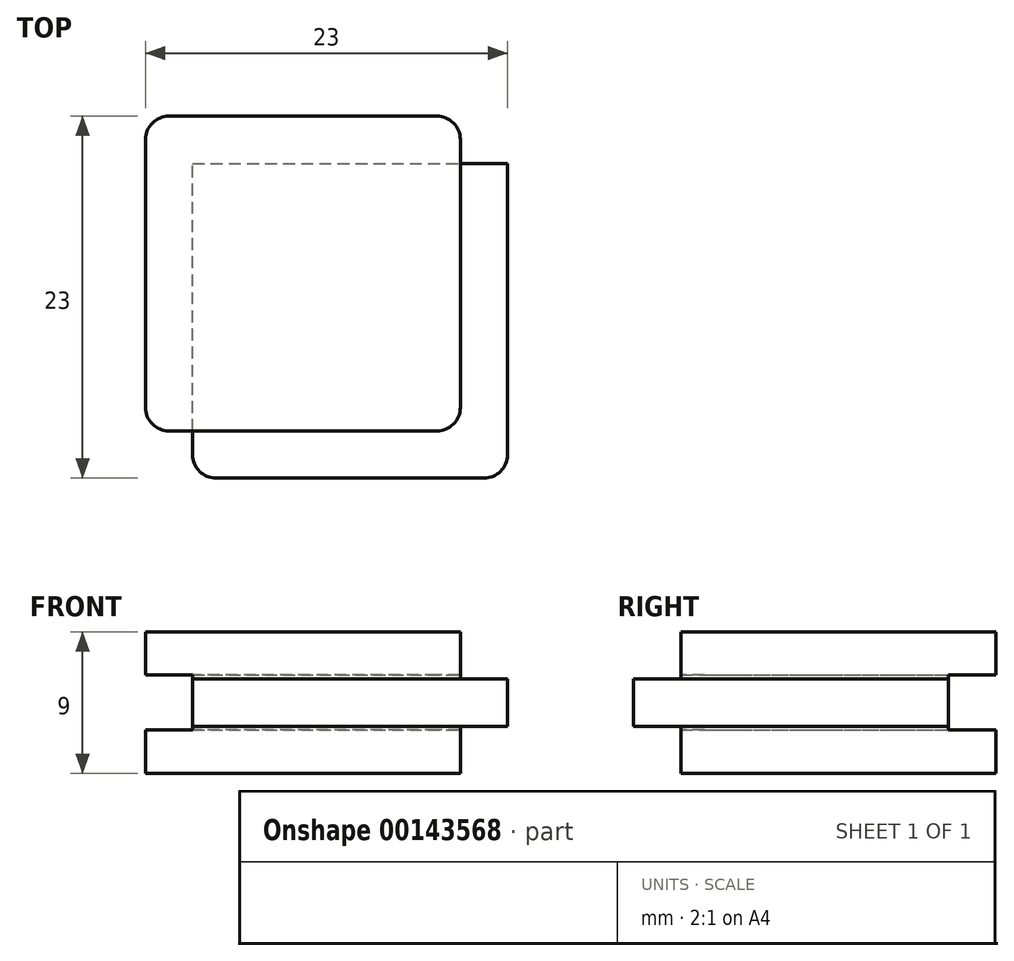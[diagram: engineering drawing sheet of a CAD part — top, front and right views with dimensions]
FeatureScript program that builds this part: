
annotation { "Feature Type Name" : "Feature", "Feature Type Description" : "" }
export const myFeature = defineFeature(function(context is Context, id is Id, definition is map)
    precondition{}
    {
        {
            var Q0;
            Q0=qCreatedBy(makeId("Front.planeOp"),FACE);
            var sketch = newSketch(context, id + "F0", { "sketchPlane" : qUnion([Q0])});
            skLineSegment(sketch, "E0.bottom", {"start": v(10, 4.5) * mm, "end": v(-10, 4.5) * mm});
            skLineSegment(sketch, "E0.top", {"start": v(10, -4.5) * mm, "end": v(-10, -4.5) * mm});
            skLineSegment(sketch, "E0.left", {"start": v(10, 4.5) * mm, "end": v(10, -4.5) * mm});
            skLineSegment(sketch, "E0.right", {"start": v(-10, 4.5) * mm, "end": v(-10, -4.5) * mm});
            skPoint(sketch, "E0.middle", {"position": v(0, 0) * mm});
            skLineSegment(sketch, "E1.bottom", {"start": v(13, 1.5) * mm, "end": v(7, 1.5) * mm});
            skLineSegment(sketch, "E1.top", {"start": v(13, -1.5) * mm, "end": v(7, -1.5) * mm});
            skLineSegment(sketch, "E1.left", {"start": v(13, 1.5) * mm, "end": v(13, -1.5) * mm});
            skLineSegment(sketch, "E1.right", {"start": v(7, 1.5) * mm, "end": v(7, -1.5) * mm});
            skPoint(sketch, "E1.middle", {"position": v(10, 0) * mm});
            skLineSegment(sketch, "E2.bottom", {"start": v(7, 1.5) * mm, "end": v(-7, 1.5) * mm});
            skLineSegment(sketch, "E2.top", {"start": v(7, -1.5) * mm, "end": v(-7, -1.5) * mm});
            skLineSegment(sketch, "E2.right", {"start": v(-7, 1.5) * mm, "end": v(-7, -1.5) * mm});
            skLineSegment(sketch, "E3.bottom", {"start": v(-7, -1.5) * mm, "end": v(-10, -1.5) * mm});
            skLineSegment(sketch, "E3.top", {"start": v(-7, 1.5) * mm, "end": v(-10, 1.5) * mm});
            skLineSegment(sketch, "E3.left", {"start": v(-7, -1.5) * mm, "end": v(-7, 1.5) * mm});
            skLineSegment(sketch, "E3.right", {"start": v(-10, -1.5) * mm, "end": v(-10, 1.5) * mm});
            skSolve(sketch);
        }
        {
            var Q0;
            {var subQ5=sQuery(id+"F0.wireOp",EDGE,"E0.bottom");Q0=makeQuery(id+"F0.imprint","IMPRINT",FACE,{"disambiguationData":[TD([[makeQuery(id+"F0.imprint","IMPRINT",EDGE,{"derivedFrom":subQ5}),1.0]])]});}
            var Q1;
            Q1=makeQuery(id+"F0.imprint","IMPRINT",FACE,{"disambiguationData":[TD([[makeQuery(id+"F0.imprint","IMPRINT",EDGE,{"derivedFrom":sQuery(id+"F0.wireOp",EDGE,"E2.bottom")}),1.0]])]});
            var Q2;
            {var subQ5=sQuery(id+"F0.wireOp",EDGE,"E1.left");Q2=makeQuery(id+"F0.imprint","IMPRINT",FACE,{"disambiguationData":[TD([[makeQuery(id+"F0.imprint","IMPRINT",EDGE,{"derivedFrom":subQ5}),-1.0]])]});}
            var Q3;
            {var subQ5=sQuery(id+"F0.wireOp",EDGE,"E1.right");Q3=makeQuery(id+"F0.imprint","IMPRINT",FACE,{"disambiguationData":[TD([[makeQuery(id+"F0.imprint","IMPRINT",EDGE,{"derivedFrom":subQ5}),1.0]])]});}
            var Q4;
            Q4=makeQuery(id+"F0.imprint","IMPRINT",FACE,{"disambiguationData":[TD([[makeQuery(id+"F0.imprint","IMPRINT",EDGE,{"derivedFrom":sQuery(id+"F0.wireOp",EDGE,"E3.bottom")}),-1.0]])]});
            var Q5;
            {var subQ5=sQuery(id+"F0.wireOp",EDGE,"E0.top");Q5=makeQuery(id+"F0.imprint","IMPRINT",FACE,{"disambiguationData":[TD([[makeQuery(id+"F0.imprint","IMPRINT",EDGE,{"derivedFrom":subQ5}),-1.0]])]});}
            extrude(context, id + "F1", {"entities" : qUnion([Q0, Q1, Q2, Q3, Q4, Q5]), "oppositeDirection" : true, "depth" : 20 * mm});
        }
        {
            var Q0;
            Q0=makeQuery(id+"F0.imprint","IMPRINT",FACE,{"disambiguationData":[TD([[makeQuery(id+"F0.imprint","IMPRINT",EDGE,{"derivedFrom":sQuery(id+"F0.wireOp",EDGE,"E3.bottom")}),-1.0]])]});
            var Q1;
            Q1=makeQuery(id+"F0.imprint","IMPRINT",FACE,{"disambiguationData":[TD([[makeQuery(id+"F0.imprint","IMPRINT",EDGE,{"derivedFrom":sQuery(id+"F0.wireOp",EDGE,"E2.bottom")}),1.0]])]});
            var Q2;
            {var subQ5=sQuery(id+"F0.wireOp",EDGE,"E1.right");Q2=makeQuery(id+"F0.imprint","IMPRINT",FACE,{"disambiguationData":[TD([[makeQuery(id+"F0.imprint","IMPRINT",EDGE,{"derivedFrom":subQ5}),1.0]])]});}
            var Q3;
            {var subQ5=sQuery(id+"F0.wireOp",EDGE,"E1.left");Q3=makeQuery(id+"F0.imprint","IMPRINT",FACE,{"disambiguationData":[TD([[makeQuery(id+"F0.imprint","IMPRINT",EDGE,{"derivedFrom":subQ5}),-1.0]])]});}
            extrude(context, id + "F2", {"entities" : qUnion([Q0, Q1, Q2, Q3]), "operationType" : NewBodyOperationType.ADD, "depth" : 3 * mm});
        }
        {
            var Q0;
            {var subQ0=sQuery(id+"F0.wireOp",EDGE,"E1.left");Q0=makeQuery(id+"F2.boolean.opBoolean","MERGE",FACE,{"derivedFrom":[makeQuery(id+"F1.opExtrude","SWEPT_FACE",FACE,{"disambiguationData":[OSD([subQ0])]}),makeQuery(id+"F2.opExtrude","SWEPT_FACE",FACE,{"disambiguationData":[OSD([subQ0])]})]});}
            var sketch = newSketch(context, id + "F3", { "sketchPlane" : qUnion([Q0])});
            skLineSegment(sketch, "E4.bottom", {"start": v(23, 1.75) * mm, "end": v(17, 1.75) * mm});
            skLineSegment(sketch, "E4.top", {"start": v(23, -1.75) * mm, "end": v(17, -1.75) * mm});
            skLineSegment(sketch, "E4.left", {"start": v(23, 1.75) * mm, "end": v(23, -1.75) * mm});
            skLineSegment(sketch, "E4.right", {"start": v(17, 1.75) * mm, "end": v(17, -1.75) * mm});
            skPoint(sketch, "E4.middle", {"position": v(20, 0) * mm});
            skSolve(sketch);
        }
        {
            var Q0;
            {var subQ1=sQuery(id+"F3.wireOp",EDGE,"E4.bottom");Q0=makeQuery(id+"F3.imprint","IMPRINT",FACE,{"disambiguationData":[TD([[makeQuery(id+"F3.imprint","IMPRINT",EDGE,{"derivedFrom":subQ1}),1.0]])]});}
            var Q1;
            {var subQ1=sQuery(id+"F0.wireOp",EDGE,"E1.left");var subQ8=makeQuery(id+"F1.opExtrude","CAP_EDGE",EDGE,{"disambiguationData":[OSD([subQ1])],"isStart":false});Q1=makeQuery(id+"F3.imprint","IMPRINT",FACE,{"disambiguationData":[TD([[makeQuery(id+"F3.imprint","IMPRINT",EDGE,{"derivedFrom":subQ8}),-1.0]])]});}
            extrude(context, id + "F4", {"entities" : qUnion([Q0, Q1]), "operationType" : NewBodyOperationType.REMOVE, "oppositeDirection" : true, "depth" : 100 * mm});
        }
        {
            var Q0;
            Q0=makeQuery(id+"F4.boolean.opBoolean","COPY",FACE,{"derivedFrom":makeQuery(id+"F4.opExtrude","SWEPT_FACE",FACE,{"disambiguationData":[OSD([sQuery(id+"F3.wireOp",EDGE,"E4.right")])]})});
            var sketch = newSketch(context, id + "F5", { "sketchPlane" : qUnion([Q0])});
            skLineSegment(sketch, "E5.bottom", {"start": v(13, 1.75) * mm, "end": v(7, 1.75) * mm});
            skLineSegment(sketch, "E5.top", {"start": v(13, -1.75) * mm, "end": v(7, -1.75) * mm});
            skLineSegment(sketch, "E5.left", {"start": v(13, 1.75) * mm, "end": v(13, -1.75) * mm});
            skLineSegment(sketch, "E5.right", {"start": v(7, 1.75) * mm, "end": v(7, -1.75) * mm});
            skPoint(sketch, "E5.middle", {"position": v(10, 0) * mm});
            skSolve(sketch);
        }
        {
            var Q0;
            {var subQ3=sQuery(id+"F5.wireOp",EDGE,"E5.left");Q0=makeQuery(id+"F5.imprint","IMPRINT",FACE,{"disambiguationData":[TD([[makeQuery(id+"F5.imprint","IMPRINT",EDGE,{"derivedFrom":subQ3}),-1.0]])]});}
            var Q1;
            {var subQ4=sQuery(id+"F5.wireOp",EDGE,"E5.right");Q1=makeQuery(id+"F5.imprint","IMPRINT",FACE,{"disambiguationData":[TD([[makeQuery(id+"F5.imprint","IMPRINT",EDGE,{"derivedFrom":subQ4}),1.0]])]});}
            extrude(context, id + "F6", {"entities" : qUnion([Q0, Q1]), "operationType" : NewBodyOperationType.REMOVE, "oppositeDirection" : true, "depth" : 100 * mm});
        }
        {
            var Q0;
            Q0=makeQuery(id+"F6.boolean.opBoolean","INTERSECT",EDGE,{"derivedFrom":[makeQuery(id+"F2.opExtrude","CAP_FACE",FACE,{"disambiguationData":[OSD([sQuery(id+"F0.wireOp",EDGE,"E1.bottom"),sQuery(id+"F0.wireOp",EDGE,"E1.top"),sQuery(id+"F0.wireOp",EDGE,"E1.left"),sQuery(id+"F0.wireOp",EDGE,"E2.bottom"),sQuery(id+"F0.wireOp",EDGE,"E2.top"),sQuery(id+"F0.wireOp",EDGE,"E3.bottom"),sQuery(id+"F0.wireOp",EDGE,"E3.top"),sQuery(id+"F0.wireOp",EDGE,"E3.right")])],"isStart":false}),makeQuery(id+"F6.opExtrude","SWEPT_FACE",FACE,{"disambiguationData":[OSD([sQuery(id+"F5.wireOp",EDGE,"E5.right")])]})]});
            var Q1;
            Q1=makeQuery(id+"F2.opExtrude","CAP_EDGE",EDGE,{"disambiguationData":[OSD([sQuery(id+"F0.wireOp",EDGE,"E1.left")])],"isStart":false});
            var Q2;
            {var subQ0=sQuery(id+"F0.wireOp",EDGE,"E0.left");Q2=makeQuery(id+"F1.opExtrude","CAP_EDGE",EDGE,{"disambiguationData":[OSD([subQ0]),TDD([makeQuery(id+"F0.imprint","IMPRINT",EDGE,{"disambiguationData":[TD([[makeQuery(id+"F0.imprint","INTERSECT",VERTEX,{"derivedFrom":[sQuery(id+"F0.wireOp",EDGE,"E0.bottom"),subQ0]}),-1.0]])],"derivedFrom":subQ0})])],"isStart":true});}
            var Q3;
            {var subQ0=sQuery(id+"F0.wireOp",EDGE,"E0.left");Q3=makeQuery(id+"F1.opExtrude","CAP_EDGE",EDGE,{"disambiguationData":[OSD([subQ0]),TDD([makeQuery(id+"F0.imprint","IMPRINT",EDGE,{"disambiguationData":[TD([[makeQuery(id+"F0.imprint","INTERSECT",VERTEX,{"derivedFrom":[sQuery(id+"F0.wireOp",EDGE,"E0.top"),subQ0]}),1.0]])],"derivedFrom":subQ0})])],"isStart":true});}
            var Q4;
            {var subQ0=sQuery(id+"F0.wireOp",EDGE,"E3.right");var subQ1=sQuery(id+"F0.wireOp",EDGE,"E0.right");var subQ3=sQuery(id+"F0.wireOp",EDGE,"E0.top");Q4=makeQuery(id+"F2.boolean.opBoolean","SPLIT",EDGE,{"disambiguationData":[TD([makeQuery(id+"F1.opExtrude","SWEPT_FACE",FACE,{"disambiguationData":[OSD([subQ3])]})])],"derivedFrom":makeQuery(id+"F1.opExtrude","CAP_EDGE",EDGE,{"disambiguationData":[OSD([subQ1,subQ0])],"isStart":true})});}
            var Q5;
            {var subQ1=sQuery(id+"F0.wireOp",EDGE,"E3.right");var subQ2=sQuery(id+"F0.wireOp",EDGE,"E0.right");var subQ3=sQuery(id+"F0.wireOp",EDGE,"E0.bottom");Q5=makeQuery(id+"F2.boolean.opBoolean","SPLIT",EDGE,{"disambiguationData":[TD([makeQuery(id+"F1.opExtrude","SWEPT_FACE",FACE,{"disambiguationData":[OSD([subQ3])]})])],"derivedFrom":makeQuery(id+"F1.opExtrude","CAP_EDGE",EDGE,{"disambiguationData":[OSD([subQ2,subQ1])],"isStart":true})});}
            var Q6;
            Q6=makeQuery(id+"F6.boolean.opBoolean","COPY",EDGE,{"derivedFrom":makeQuery(id+"F6.opExtrude","CAP_EDGE",EDGE,{"disambiguationData":[OSD([sQuery(id+"F5.wireOp",EDGE,"E5.right")])],"isStart":true})});
            var Q7;
            {var subQ0=sQuery(id+"F0.wireOp",EDGE,"E3.right");var subQ1=sQuery(id+"F0.wireOp",EDGE,"E0.right");var subQ2=sQuery(id+"F0.wireOp",EDGE,"E0.bottom");Q7=makeQuery(id+"F4.boolean.opBoolean","SPLIT",EDGE,{"disambiguationData":[TD([makeQuery(id+"F1.opExtrude","SWEPT_FACE",FACE,{"disambiguationData":[OSD([subQ2])]})])],"derivedFrom":makeQuery(id+"F1.opExtrude","CAP_EDGE",EDGE,{"disambiguationData":[OSD([subQ1,subQ0])],"isStart":false})});}
            var Q8;
            {var subQ0=sQuery(id+"F0.wireOp",EDGE,"E3.right");var subQ1=sQuery(id+"F0.wireOp",EDGE,"E0.right");var subQ2=sQuery(id+"F0.wireOp",EDGE,"E0.top");Q8=makeQuery(id+"F4.boolean.opBoolean","SPLIT",EDGE,{"disambiguationData":[TD([makeQuery(id+"F1.opExtrude","SWEPT_FACE",FACE,{"disambiguationData":[OSD([subQ2])]})])],"derivedFrom":makeQuery(id+"F1.opExtrude","CAP_EDGE",EDGE,{"disambiguationData":[OSD([subQ1,subQ0])],"isStart":false})});}
            var Q9;
            Q9=makeQuery(id+"F4.boolean.opBoolean","COPY",EDGE,{"derivedFrom":makeQuery(id+"F4.opExtrude","CAP_EDGE",EDGE,{"disambiguationData":[OSD([sQuery(id+"F3.wireOp",EDGE,"E4.right")])],"isStart":true})});
            var Q10;
            {var subQ0=sQuery(id+"F0.wireOp",EDGE,"E0.left");Q10=makeQuery(id+"F1.opExtrude","CAP_EDGE",EDGE,{"disambiguationData":[OSD([subQ0]),TDD([makeQuery(id+"F0.imprint","IMPRINT",EDGE,{"disambiguationData":[TD([[makeQuery(id+"F0.imprint","INTERSECT",VERTEX,{"derivedFrom":[sQuery(id+"F0.wireOp",EDGE,"E0.bottom"),subQ0]}),-1.0]])],"derivedFrom":subQ0})])],"isStart":false});}
            var Q11;
            {var subQ0=sQuery(id+"F0.wireOp",EDGE,"E0.left");Q11=makeQuery(id+"F1.opExtrude","CAP_EDGE",EDGE,{"disambiguationData":[OSD([subQ0]),TDD([makeQuery(id+"F0.imprint","IMPRINT",EDGE,{"disambiguationData":[TD([[makeQuery(id+"F0.imprint","INTERSECT",VERTEX,{"derivedFrom":[sQuery(id+"F0.wireOp",EDGE,"E0.top"),subQ0]}),1.0]])],"derivedFrom":subQ0})])],"isStart":false});}
            fillet(context, id + "F7", {"entities" : qUnion([Q0, Q1, Q2, Q3, Q4, Q5, Q6, Q7, Q8, Q9, Q10, Q11]), "radius" : 1.5 * mm, "tangentPropagation" : true, "allowEdgeOverflow" : false});
        }
    });
